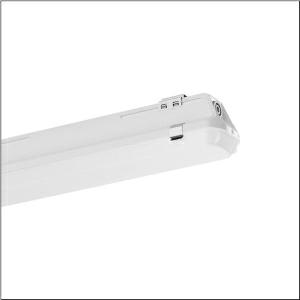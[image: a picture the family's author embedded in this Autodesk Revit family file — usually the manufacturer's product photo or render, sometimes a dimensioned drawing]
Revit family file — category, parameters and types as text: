
# Revit family: monsun_r__21_51fb10mp380b_1725
name_source: partatom
category: Lighting Fixtures
units: mm (PartAtom-declared; Revit-internal decimal feet)

## family parameters
Cut with Voids When Loaded = No
Host = Face
Light Source = No
Part Type = Normal
Room Calculation Point = No
Round Connector Dimension = Use Diameter
Shared = No

## types (1)
- --- (1 x LED, 8190 lm, 59.7 W, 3000K)
    Apparent Load = 60 VA
    CIE Flux Codes = 47 77 93 94 100
    Color Rendering = 80
    Color Temperature = 3000K
    Default Elevation = 1800 mm
    Description = Monsun® 21, damp-proof luminaire, chain hanger, primary optical cover: enclosure, of PMMA, light emission: direct distribution, primary light characteristic: symmetric, installation type: suspended mounting, surface-mounted, horizontal mounting, vertical mounting, LED, rated luminous flux: 8.190lm, luminous efficacy: 153lm/W, light colour: 830, colour temperature: 3000K, control gear: ECG, with terminal, 3-pole, max. 2.5mm², mains connection: 220..240V, AC, 50/60Hz, rated input power: 54W, housing, of glass-fibre reinforced polyester, uncoated, bright grey, incl. chain hanger, length: 1.590mm, width: 90mm, height: 88mm, clip for enclosure, of stainless steel (V2A), ceiling mounting element, of stainless steel (V2A), chain hanger, of stainless steel (V2A), protection rating (complete): IP66, insulation class (complete): insulation class I (protective earthing), certification: CE, ENEC, VDE, UKCA, protection symbol: D, impact resistance: IK04, permissible operating ambient temperature: -25..+35°C, standard: EN 50419, EN 60598-2-1, no direct snow, no direct sun, no direct rain, for indoor or canopied outdoor use, corresponds to IFS (International Featured Standards) requirements for safety and quality in the food industry, contact your sales advisor before using the luminaires in applications with unclear chemical exposure, large temperature fluctuations or condensation-forming humidity, LABS conformity tested according to VDMA 24364:2018-05, packaging unit: 1 piece
    Height = 89 mm
    Lamp = 1 x LED
    Lamp Light Flux = 8190 lm
    Lamp Power = 59.7 W
    Lamp count = 1
    Length = 1590 mm
    Luminous efficacy = 137 lm/W
    Manufacturer = Siteco
    ModVariant = No
    Model = 51FB10MP380B
    Mounting Place = Ceiling
    Mounting Type = Surface mounted
    Number of Poles = 1
    OnlyDefault = Yes
    Power Factor = 1
    Product Name = Monsun® 21
    Product group = damp-proof luminaire
    ProductGroupID = 301
    Protection Class = Protection class I
    Protection Degree = IP 66
    RLX_Detail_Level = 1
    RLX_Emergency_Light_Flux = 0 lm
    RLX_Emergency_Type = 0
    RLX_Emergency_Type_DB = No
    RlxData = <blob elided: 89765 chars, md5=821767fb>
    Socket = socket
    Standby Power = 0 W
    System Light Flux = 8190 lm
    System Power = 60 W
    Type Comments = factory setting: luminous flux: 100 % | (A | C | E) | 134 mA
    Type Image = l_1006717.jpg
    URL = http://relux.com
    VarID = @adj_096579
    Voltage = 0 V
    Weight = 0.00 kg
    Width = 90 mm

## geometry (parser evidence)
native form markers: Blend x4, Sweep x13
no freeform markers — native parametric forms only
